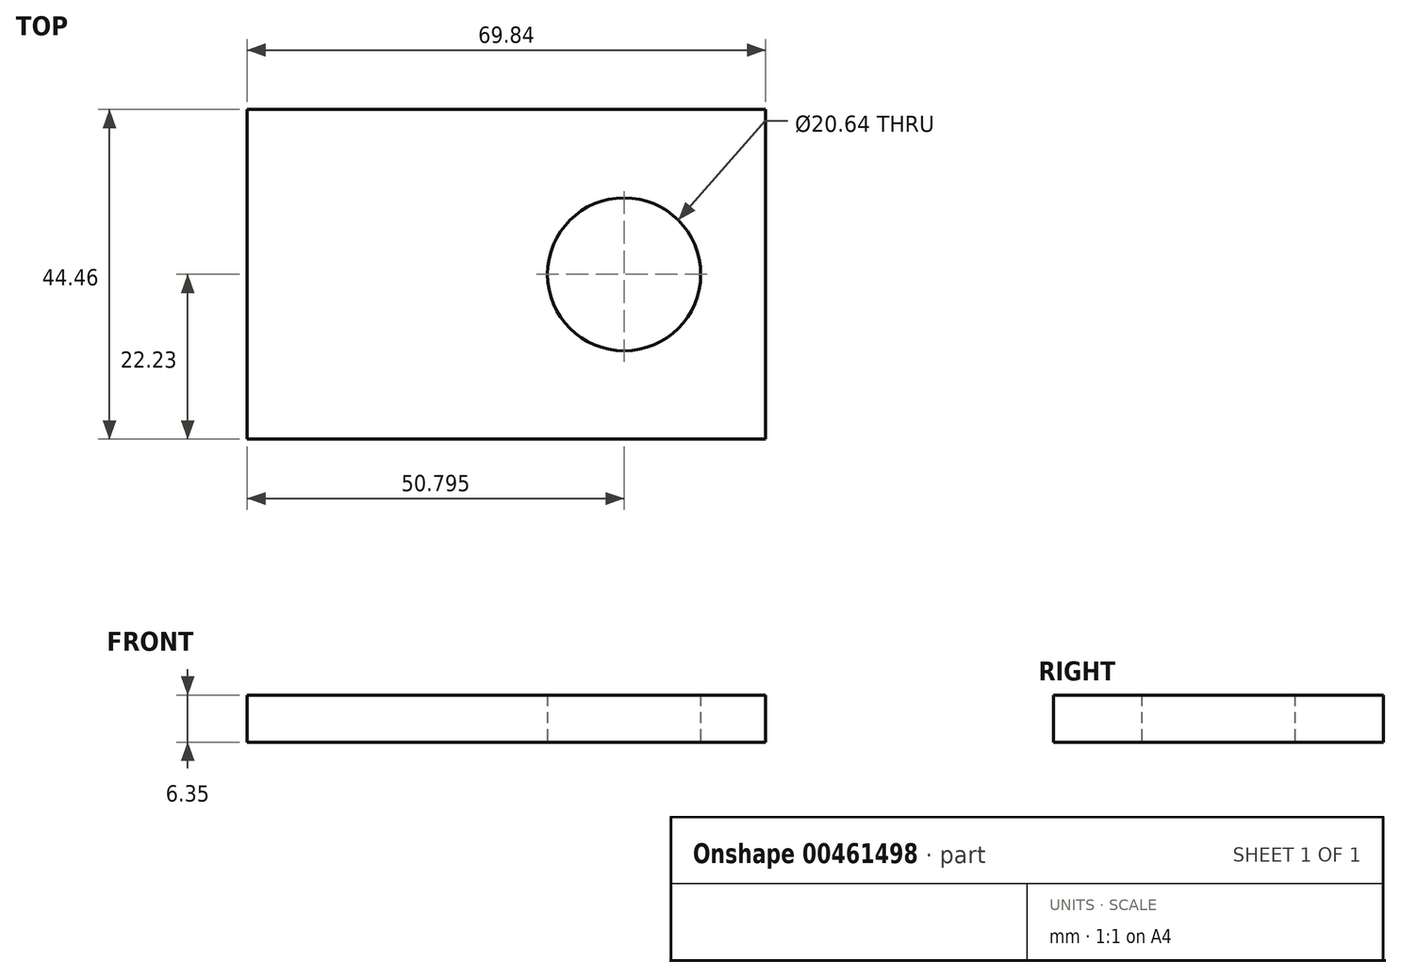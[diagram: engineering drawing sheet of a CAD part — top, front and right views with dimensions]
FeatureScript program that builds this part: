
annotation { "Feature Type Name" : "Feature", "Feature Type Description" : "" }
export const myFeature = defineFeature(function(context is Context, id is Id, definition is map)
    precondition{}
    {
        {
            var Q0;
            Q0=qCreatedBy(makeId("Top.planeOp"),FACE);
            var sketch = newSketch(context, id + "F0", { "sketchPlane" : qUnion([Q0])});
            skLineSegment(sketch, "E0.bottom", {"start": v(34.93, -22.22) * mm, "end": v(-34.93, -22.23) * mm});
            skLineSegment(sketch, "E0.top", {"start": v(34.93, 22.23) * mm, "end": v(-34.93, 22.22) * mm});
            skLineSegment(sketch, "E0.left", {"start": v(34.93, -22.22) * mm, "end": v(34.93, 22.23) * mm});
            skLineSegment(sketch, "E0.right", {"start": v(-34.93, -22.23) * mm, "end": v(-34.93, 22.22) * mm});
            skPoint(sketch, "E0.middle", {"position": v(0, 0) * mm});
            skCircle(sketch, "E1", {"center": v(15.88, 0) * mm, "radius": 10.32 * mm});
            skSolve(sketch);
        }
        {
            var Q0;
            Q0 = qSketchRegion(id + "F0", true);
            extrude(context, id + "F1", {"entities" : qUnion([Q0]), "depth" : 6.35 * mm});
        }
    });
